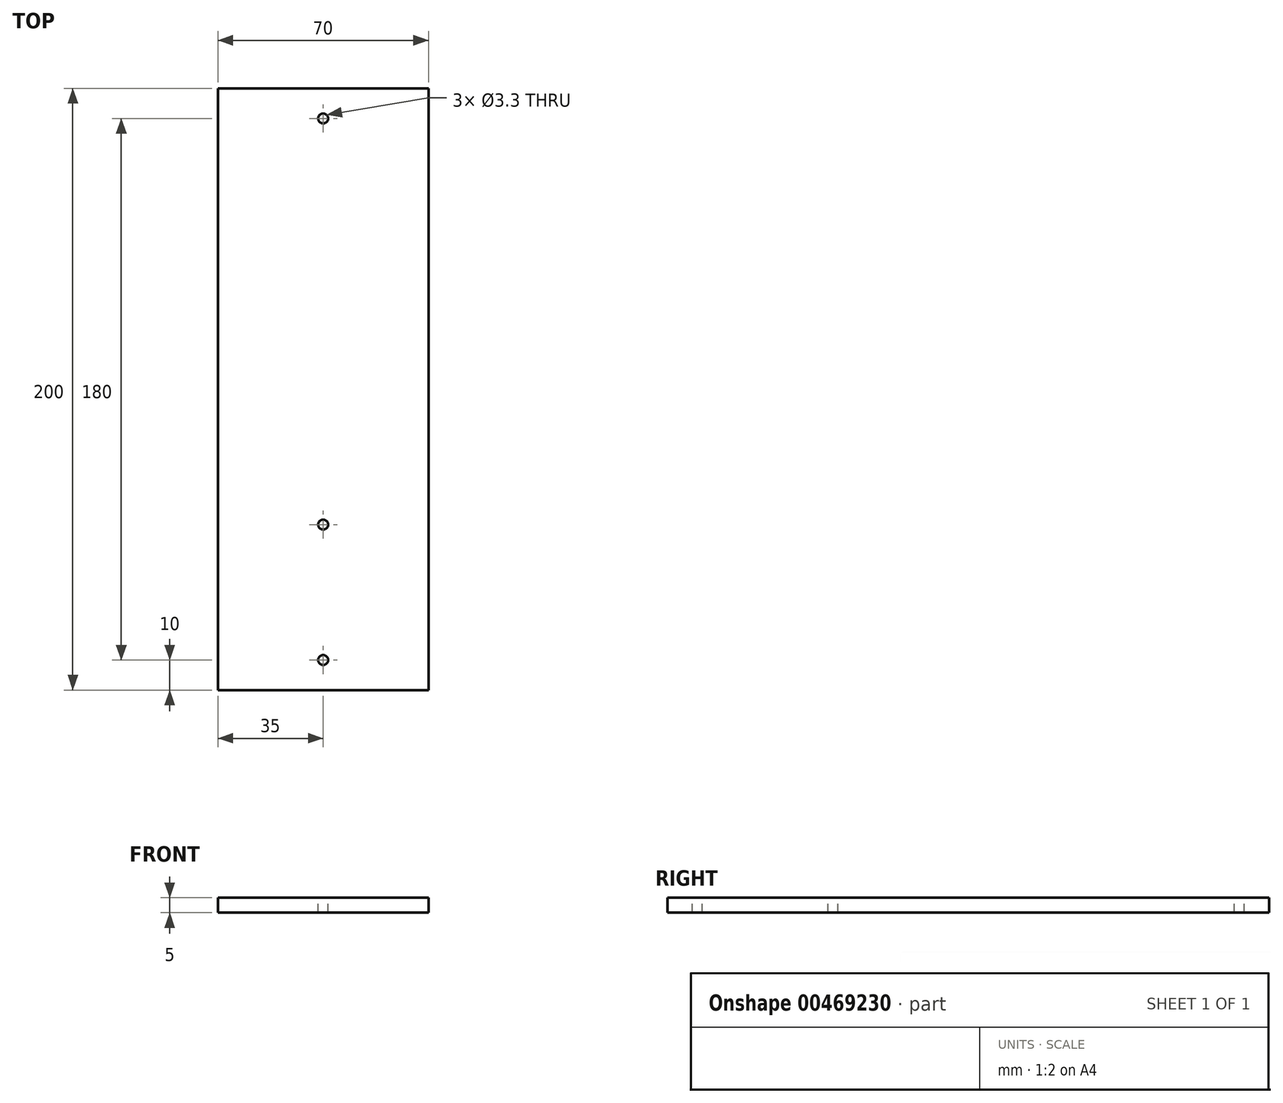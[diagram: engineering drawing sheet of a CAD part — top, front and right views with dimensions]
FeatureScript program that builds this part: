
annotation { "Feature Type Name" : "Feature", "Feature Type Description" : "" }
export const myFeature = defineFeature(function(context is Context, id is Id, definition is map)
    precondition{}
    {
        {
            var Q0;
            Q0=qCreatedBy(makeId("Top.planeOp"),FACE);
            var sketch = newSketch(context, id + "F0", { "sketchPlane" : qUnion([Q0])});
            skLineSegment(sketch, "E0.bottom", {"start": v(0, 0) * mm, "end": v(70, 0) * mm});
            skLineSegment(sketch, "E0.top", {"start": v(0, 200) * mm, "end": v(70, 200) * mm});
            skLineSegment(sketch, "E0.left", {"start": v(0, 0) * mm, "end": v(0, 200) * mm});
            skLineSegment(sketch, "E0.right", {"start": v(70, 0) * mm, "end": v(70, 200) * mm});
            skSolve(sketch);
        }
        {
            var Q0;
            Q0=qSketchRegion(id+"F0",true);
            extrude(context, id + "F1", {"entities" : qUnion([Q0]), "depth" : 5 * mm});
        }
        {
            var Q0;
            Q0=makeQuery(id+"F1.opExtrude","CAP_FACE",FACE,{"disambiguationData":[OSD([sQuery(id+"F0.wireOp",EDGE,"E0.bottom"),sQuery(id+"F0.wireOp",EDGE,"E0.top"),sQuery(id+"F0.wireOp",EDGE,"E0.left"),sQuery(id+"F0.wireOp",EDGE,"E0.right")])],"isStart":false});
            var sketch = newSketch(context, id + "F2", { "sketchPlane" : qUnion([Q0])});
            skLineSegment(sketch, "E1", {"start": v(35, 200) * mm, "end": v(35, 0) * mm, "construction": true});
            skPoint(sketch, "E2", {"position": v(35, 10) * mm});
            skPoint(sketch, "E3", {"position": v(35, 55) * mm});
            skPoint(sketch, "E4", {"position": v(35, 190) * mm});
            skSolve(sketch);
        }
        {
            var Q0;
            Q0=sQuery(id+"F2.wireOp",VERTEX,"E4");
            var Q1;
            Q1=sQuery(id+"F2.wireOp",VERTEX,"E3");
            var Q2;
            Q2=sQuery(id+"F2.wireOp",VERTEX,"E2");
            var Q3;
            Q3=makeQuery(id+"F1.opExtrude","SWEPT_BODY",BODY,{"disambiguationData":[OSD([sQuery(id+"F0.wireOp",EDGE,"E0.bottom"),sQuery(id+"F0.wireOp",EDGE,"E0.top"),sQuery(id+"F0.wireOp",EDGE,"E0.left"),sQuery(id+"F0.wireOp",EDGE,"E0.right")])]});
            hole(context, id + "F3", {"style" : HoleStyle.SIMPLE, "endStyle" : HoleEndStyle.THROUGH, "standardTappedOrClearance" : lookupTablePath({ "standard" : "ISO", "fit" : "Normal", "size" : "M3", "type" : "Clearance" }), "standardBlindInLast" : lookupTablePath({ "fit" : "Standard", "standard" : "ISO", "size" : "M3", "type" : "Clearance" }), "holeDiameter" : 3.3 * mm, "isTappedThrough" : true, "tappedDepth" : 12 * mm, "tapClearance" : 3, "locations" : qUnion([Q0, Q1, Q2]), "scope" : qUnion([Q3])});
        }
    });
